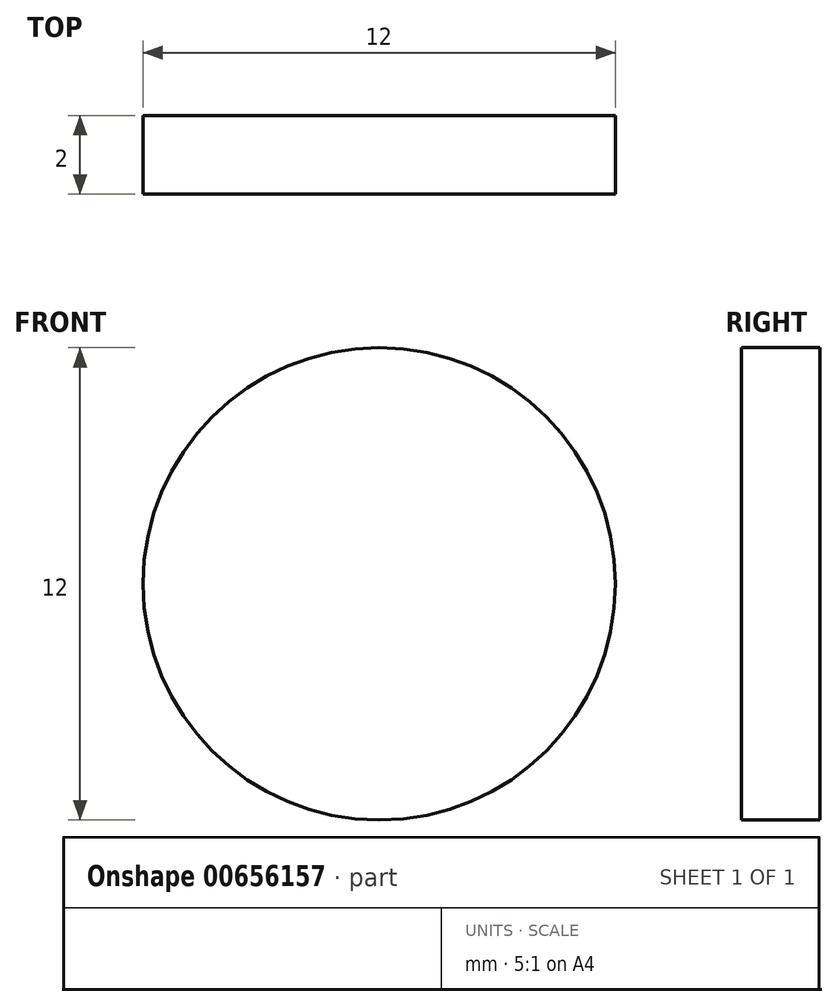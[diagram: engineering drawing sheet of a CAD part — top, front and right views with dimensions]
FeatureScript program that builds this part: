
annotation { "Feature Type Name" : "Feature", "Feature Type Description" : "" }
export const myFeature = defineFeature(function(context is Context, id is Id, definition is map)
    precondition{}
    {
        {
            var Q0;
            Q0=qCreatedBy(makeId("Front.planeOp"),FACE);
            var sketch = newSketch(context, id + "F0", { "sketchPlane" : qUnion([Q0])});
            skCircle(sketch, "E0", {"center": v(0, 0) * mm, "radius": 6 * mm});
            skSolve(sketch);
        }
        {
            var Q0;
            Q0=makeQuery(id+"F0.imprint","IMPRINT",FACE,{"disambiguationData":[TD([[makeQuery(id+"F0.imprint","IMPRINT",EDGE,{"derivedFrom":sQuery(id+"F0.wireOp",EDGE,"E0")}),1.0]])]});
            extrude(context, id + "F1", {"entities" : qUnion([Q0]), "endBound" : BoundingType.SYMMETRIC, "depth" : 2 * mm, "offsetDistance" : 25 * mm});
        }
    });
